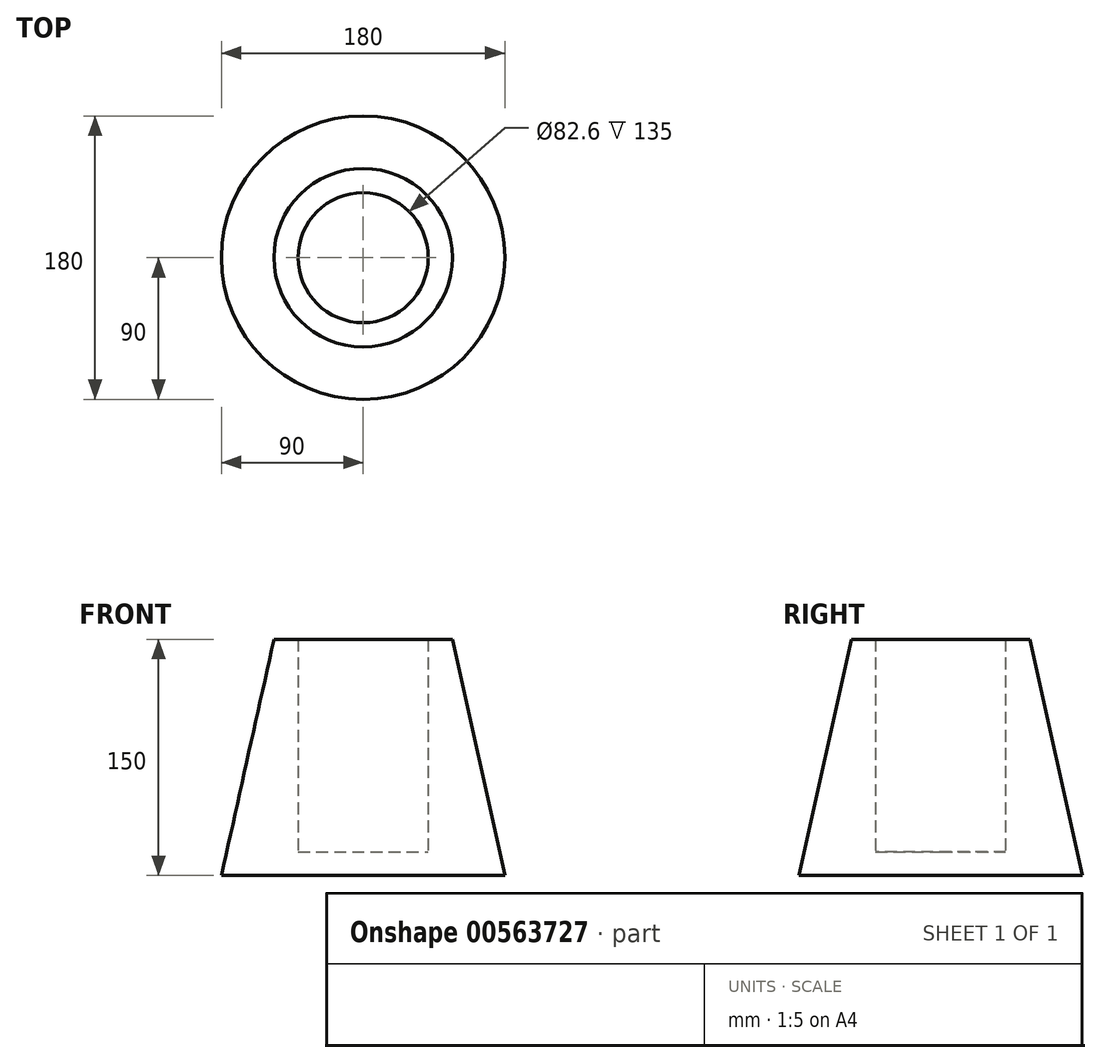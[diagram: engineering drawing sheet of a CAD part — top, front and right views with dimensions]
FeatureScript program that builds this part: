
annotation { "Feature Type Name" : "Feature", "Feature Type Description" : "" }
export const myFeature = defineFeature(function(context is Context, id is Id, definition is map)
    precondition{}
    {
        {
            var Q0;
            Q0=qCreatedBy(makeId("Front.planeOp"),FACE);
            var sketch = newSketch(context, id + "F0", { "sketchPlane" : qUnion([Q0])});
            skLineSegment(sketch, "E0", {"start": v(0, 0) * mm, "end": v(90, 0) * mm});
            skLineSegment(sketch, "E1", {"start": v(0, 0) * mm, "end": v(0, 15) * mm});
            skLineSegment(sketch, "E2", {"start": v(0, 0) * mm, "end": v(0, 180) * mm, "construction": true});
            skLineSegment(sketch, "E3", {"start": v(0, 180) * mm, "end": v(50, 180) * mm, "construction": true});
            skLineSegment(sketch, "E4", {"start": v(90, 0) * mm, "end": v(50, 180) * mm, "construction": true});
            skLineSegment(sketch, "E5", {"start": v(0, 15) * mm, "end": v(86.67, 15) * mm, "construction": true});
            skLineSegment(sketch, "E6", {"start": v(50, 180) * mm, "end": v(34.63, 180) * mm});
            skLineSegment(sketch, "E7", {"start": v(71.3, 15) * mm, "end": v(0, 15) * mm});
            skLineSegment(sketch, "E8", {"start": v(0, 0) * mm, "end": v(0, 150) * mm, "construction": true});
            skLineSegment(sketch, "E9", {"start": v(0, 150) * mm, "end": v(56.67, 150) * mm, "construction": true});
            skLineSegment(sketch, "E10", {"start": v(56.67, 150) * mm, "end": v(41.3, 150) * mm});
            skLineSegment(sketch, "E11", {"start": v(56.67, 150) * mm, "end": v(90, 0) * mm});
            skLineSegment(sketch, "E12", {"start": v(41.3, 150) * mm, "end": v(71.3, 15) * mm, "construction": true});
            skLineSegment(sketch, "E13", {"start": v(41.3, 150) * mm, "end": v(41.3, 15) * mm});
            skSolve(sketch);
        }
        {
            var Q0;
            Q0=makeQuery(id+"F0.imprint","IMPRINT",FACE,{"disambiguationData":[TD([[makeQuery(id+"F0.imprint","IMPRINT",EDGE,{"derivedFrom":sQuery(id+"F0.wireOp",EDGE,"E0")}),1.0]])]});
            var Q1;
            Q1=sQuery(id+"F0.wireOp",EDGE,"E8");
            revolve(context, id + "F1", {"entities" : qUnion([Q0]), "axis" : qUnion([Q1]), "revolveType" : RevolveType.FULL});
        }
    });
